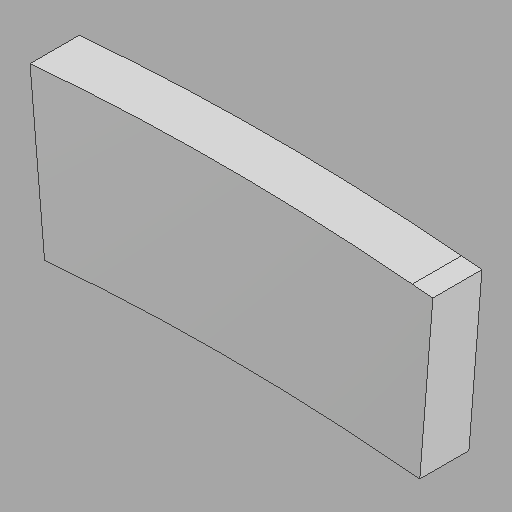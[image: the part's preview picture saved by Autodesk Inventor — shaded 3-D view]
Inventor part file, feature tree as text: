
AUTODESK INVENTOR PART (.ipt)
format: ipt  version: 2022.1 (Build 261234020, 234B)  size: 90,112 bytes
history: imported  units: in
note: dims shown in document units (in); Inventor stores cm internally (conversion verified against a paired STEP export)
features: imported_body x1
ambient origin geometry x8: Origin, YZ Plane, XZ Plane, XY Plane, X Axis, Y Axis, Z Axis, Center Point
bodies: Solid1 (imported_parasolid), Body1 (imported_parasolid)
feature tree (1):
  imported_body  NMx_Import_Brep_tag  [imported B-rep: ~8 faces, bbox_mm=[1249.418368, 511.657745, 152.4]]
